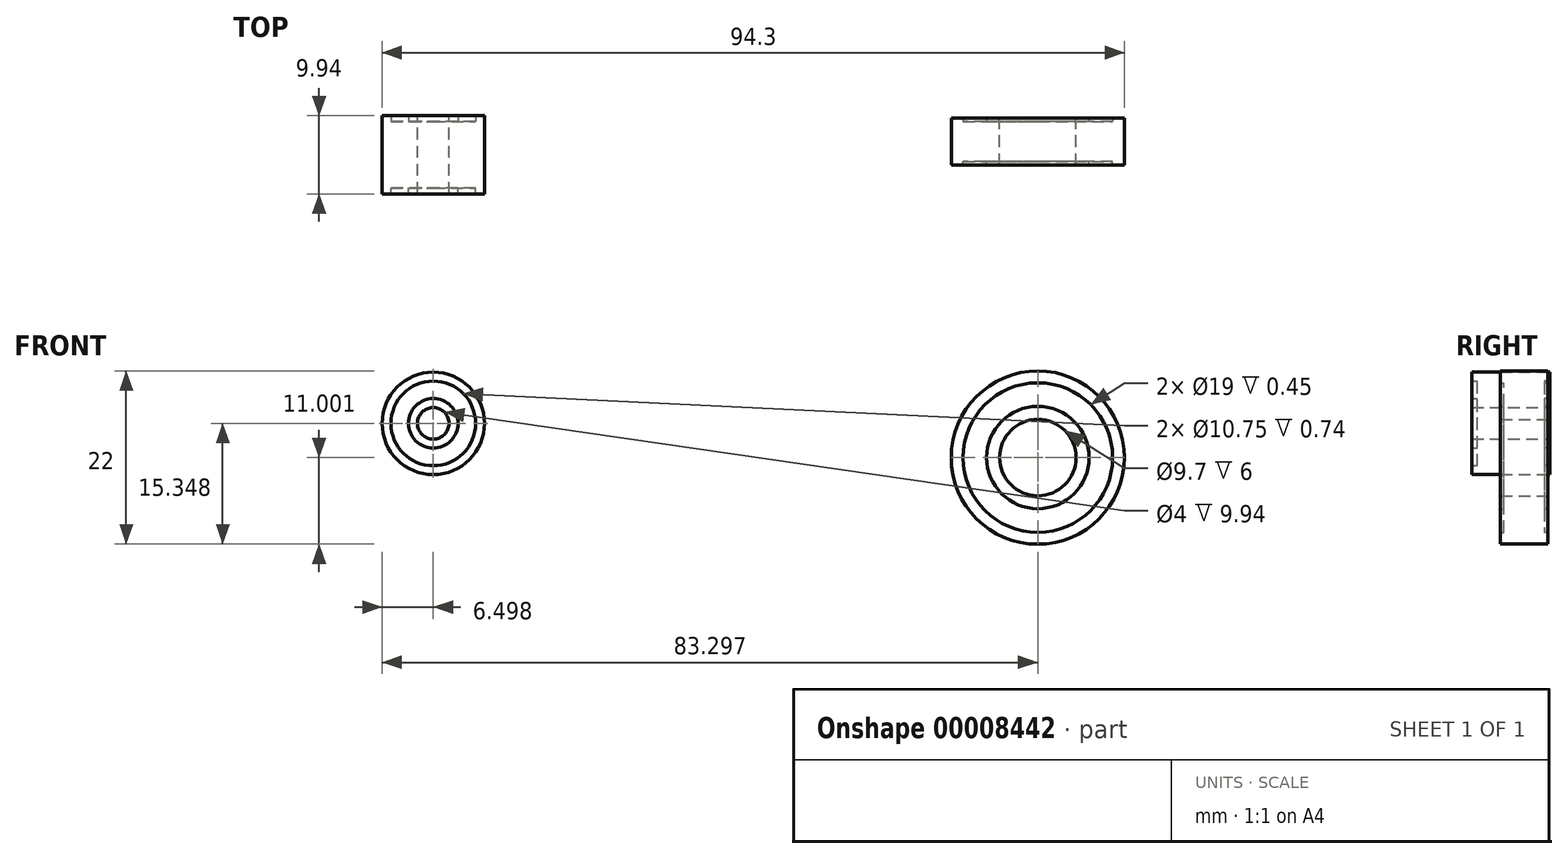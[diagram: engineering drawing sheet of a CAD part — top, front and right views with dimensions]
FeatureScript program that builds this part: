
annotation { "Feature Type Name" : "Feature", "Feature Type Description" : "" }
export const myFeature = defineFeature(function(context is Context, id is Id, definition is map)
    precondition{}
    {
        {
            var Q0;
            Q0=qCreatedBy(makeId("Front.planeOp"),FACE);
            var sketch = newSketch(context, id + "F0", { "sketchPlane" : qUnion([Q0])});
            skCircle(sketch, "E0", {"center": v(-42.2, 33.09) * mm, "radius": 6.5 * mm});
            skCircle(sketch, "E1", {"center": v(-42.2, 33.09) * mm, "radius": 2 * mm});
            skSolve(sketch);
        }
        {
            var Q0;
            Q0=makeQuery(id+"F0.imprint","IMPRINT",FACE,{"disambiguationData":[TD([[makeQuery(id+"F0.imprint","IMPRINT",EDGE,{"derivedFrom":sQuery(id+"F0.wireOp",EDGE,"E0")}),1.0]])]});
            extrude(context, id + "F1", {"entities" : qUnion([Q0]), "depth" : 8.46 * mm});
        }
        {
            var Q0;
            Q0=makeQuery(id+"F1.opExtrude","CAP_FACE",FACE,{"disambiguationData":[OSD([sQuery(id+"F0.wireOp",EDGE,"E0"),sQuery(id+"F0.wireOp",EDGE,"E1")])],"isStart":false});
            var sketch = newSketch(context, id + "F2", { "sketchPlane" : qUnion([Q0])});
            skPoint(sketch, "E2", {"position": v(-42.2, 33.09) * mm});
            skPoint(sketch, "E3", {"position": v(-42.2, 39.59) * mm});
            skPoint(sketch, "E4", {"position": v(-42.2, 35.09) * mm});
            skCircle(sketch, "E5", {"center": v(-42.2, 33.09) * mm, "radius": 2 * mm});
            skCircle(sketch, "E6", {"center": v(-42.2, 33.09) * mm, "radius": 3.15 * mm});
            skCircle(sketch, "E7", {"center": v(-42.2, 33.09) * mm, "radius": 5.38 * mm});
            skCircle(sketch, "E8", {"center": v(-42.2, 33.09) * mm, "radius": 6.5 * mm});
            skSolve(sketch);
        }
        {
            var Q0;
            Q0=makeQuery(id+"F2.imprint","IMPRINT",FACE,{"disambiguationData":[TD([[makeQuery(id+"F2.imprint","IMPRINT",EDGE,{"derivedFrom":sQuery(id+"F2.wireOp",EDGE,"E7")}),-1.0]])]});
            var Q1;
            Q1=makeQuery(id+"F2.imprint","IMPRINT",FACE,{"disambiguationData":[TD([[makeQuery(id+"F2.imprint","IMPRINT",EDGE,{"derivedFrom":sQuery(id+"F2.wireOp",EDGE,"E5")}),-1.0]])]});
            extrude(context, id + "F3", {"entities" : qUnion([Q0, Q1]), "operationType" : NewBodyOperationType.ADD, "depth" : 0.74 * mm});
        }
        {
            var Q0;
            Q0=makeQuery(id+"F1.opExtrude","CAP_FACE",FACE,{"disambiguationData":[OSD([sQuery(id+"F0.wireOp",EDGE,"E0"),sQuery(id+"F0.wireOp",EDGE,"E1")])],"isStart":true});
            var sketch = newSketch(context, id + "F4", { "sketchPlane" : qUnion([Q0])});
            skPoint(sketch, "E9", {"position": v(42.2, 33.09) * mm});
            skPoint(sketch, "E10", {"position": v(42.2, 35.09) * mm});
            skPoint(sketch, "E11", {"position": v(42.2, 39.59) * mm});
            skCircle(sketch, "E12", {"center": v(42.2, 33.09) * mm, "radius": 2 * mm});
            skCircle(sketch, "E13", {"center": v(42.2, 33.09) * mm, "radius": 3.15 * mm});
            skCircle(sketch, "E14", {"center": v(42.2, 33.09) * mm, "radius": 5.38 * mm});
            skCircle(sketch, "E15", {"center": v(42.2, 33.09) * mm, "radius": 6.5 * mm});
            skSolve(sketch);
        }
        {
            var Q0;
            Q0=makeQuery(id+"F4.imprint","IMPRINT",FACE,{"disambiguationData":[TD([[makeQuery(id+"F4.imprint","IMPRINT",EDGE,{"derivedFrom":sQuery(id+"F4.wireOp",EDGE,"E14")}),-1.0]])]});
            var Q1;
            Q1=makeQuery(id+"F4.imprint","IMPRINT",FACE,{"disambiguationData":[TD([[makeQuery(id+"F4.imprint","IMPRINT",EDGE,{"derivedFrom":sQuery(id+"F4.wireOp",EDGE,"E12")}),1.0]])]});
            extrude(context, id + "F5", {"entities" : qUnion([Q0, Q1]), "operationType" : NewBodyOperationType.ADD, "depth" : 0.74 * mm});
        }
        {
            var Q0;
            Q0=qCreatedBy(makeId("Front.planeOp"),FACE);
            var sketch = newSketch(context, id + "F6", { "sketchPlane" : qUnion([Q0])});
            skCircle(sketch, "E16", {"center": v(34.6, 28.74) * mm, "radius": 4.85 * mm});
            skCircle(sketch, "E17", {"center": v(34.6, 28.74) * mm, "radius": 11 * mm});
            skSolve(sketch);
        }
        {
            var Q0;
            Q0=makeQuery(id+"F6.imprint","IMPRINT",FACE,{"disambiguationData":[TD([[makeQuery(id+"F6.imprint","IMPRINT",EDGE,{"derivedFrom":sQuery(id+"F6.wireOp",EDGE,"E16")}),-1.0]])]});
            extrude(context, id + "F7", {"entities" : qUnion([Q0]), "depth" : 5.1 * mm});
        }
        {
            var Q0;
            Q0=makeQuery(id+"F7.opExtrude","CAP_FACE",FACE,{"disambiguationData":[OSD([sQuery(id+"F6.wireOp",EDGE,"E16"),sQuery(id+"F6.wireOp",EDGE,"E17")])],"isStart":false});
            var sketch = newSketch(context, id + "F8", { "sketchPlane" : qUnion([Q0])});
            skPoint(sketch, "E18", {"position": v(34.6, 28.74) * mm});
            skPoint(sketch, "E19", {"position": v(34.6, 33.6) * mm});
            skPoint(sketch, "E20", {"position": v(34.6, 39.74) * mm});
            skCircle(sketch, "E21", {"center": v(34.6, 28.74) * mm, "radius": 4.85 * mm});
            skCircle(sketch, "E22", {"center": v(34.6, 28.74) * mm, "radius": 6.5 * mm});
            skCircle(sketch, "E23", {"center": v(34.6, 28.74) * mm, "radius": 9.5 * mm});
            skCircle(sketch, "E24", {"center": v(34.6, 28.74) * mm, "radius": 11 * mm});
            skSolve(sketch);
        }
        {
            var Q0;
            Q0=makeQuery(id+"F8.imprint","IMPRINT",FACE,{"disambiguationData":[TD([[makeQuery(id+"F8.imprint","IMPRINT",EDGE,{"derivedFrom":sQuery(id+"F8.wireOp",EDGE,"E21")}),-1.0]])]});
            var Q1;
            Q1=makeQuery(id+"F8.imprint","IMPRINT",FACE,{"disambiguationData":[TD([[makeQuery(id+"F8.imprint","IMPRINT",EDGE,{"derivedFrom":sQuery(id+"F8.wireOp",EDGE,"E23")}),-1.0]])]});
            extrude(context, id + "F9", {"entities" : qUnion([Q0, Q1]), "operationType" : NewBodyOperationType.ADD, "depth" : 0.45 * mm});
        }
        {
            var Q0;
            Q0=makeQuery(id+"F7.opExtrude","CAP_FACE",FACE,{"disambiguationData":[OSD([sQuery(id+"F6.wireOp",EDGE,"E16"),sQuery(id+"F6.wireOp",EDGE,"E17")])],"isStart":true});
            var sketch = newSketch(context, id + "F10", { "sketchPlane" : qUnion([Q0])});
            skPoint(sketch, "E25", {"position": v(-34.6, 28.74) * mm});
            skPoint(sketch, "E26", {"position": v(-34.6, 33.6) * mm});
            skPoint(sketch, "E27", {"position": v(-34.6, 39.74) * mm});
            skCircle(sketch, "E28", {"center": v(-34.6, 28.74) * mm, "radius": 4.85 * mm});
            skCircle(sketch, "E29", {"center": v(-34.6, 28.74) * mm, "radius": 6.5 * mm});
            skCircle(sketch, "E30", {"center": v(-34.6, 28.74) * mm, "radius": 9.5 * mm});
            skCircle(sketch, "E31", {"center": v(-34.6, 28.74) * mm, "radius": 11 * mm});
            skSolve(sketch);
        }
        {
            var Q0;
            Q0=makeQuery(id+"F10.imprint","IMPRINT",FACE,{"disambiguationData":[TD([[makeQuery(id+"F10.imprint","IMPRINT",EDGE,{"derivedFrom":sQuery(id+"F10.wireOp",EDGE,"E30")}),-1.0]])]});
            var Q1;
            Q1=makeQuery(id+"F10.imprint","IMPRINT",FACE,{"disambiguationData":[TD([[makeQuery(id+"F10.imprint","IMPRINT",EDGE,{"derivedFrom":sQuery(id+"F10.wireOp",EDGE,"E28")}),1.0]])]});
            extrude(context, id + "F11", {"entities" : qUnion([Q0, Q1]), "operationType" : NewBodyOperationType.ADD, "depth" : 0.45 * mm});
        }
    });
